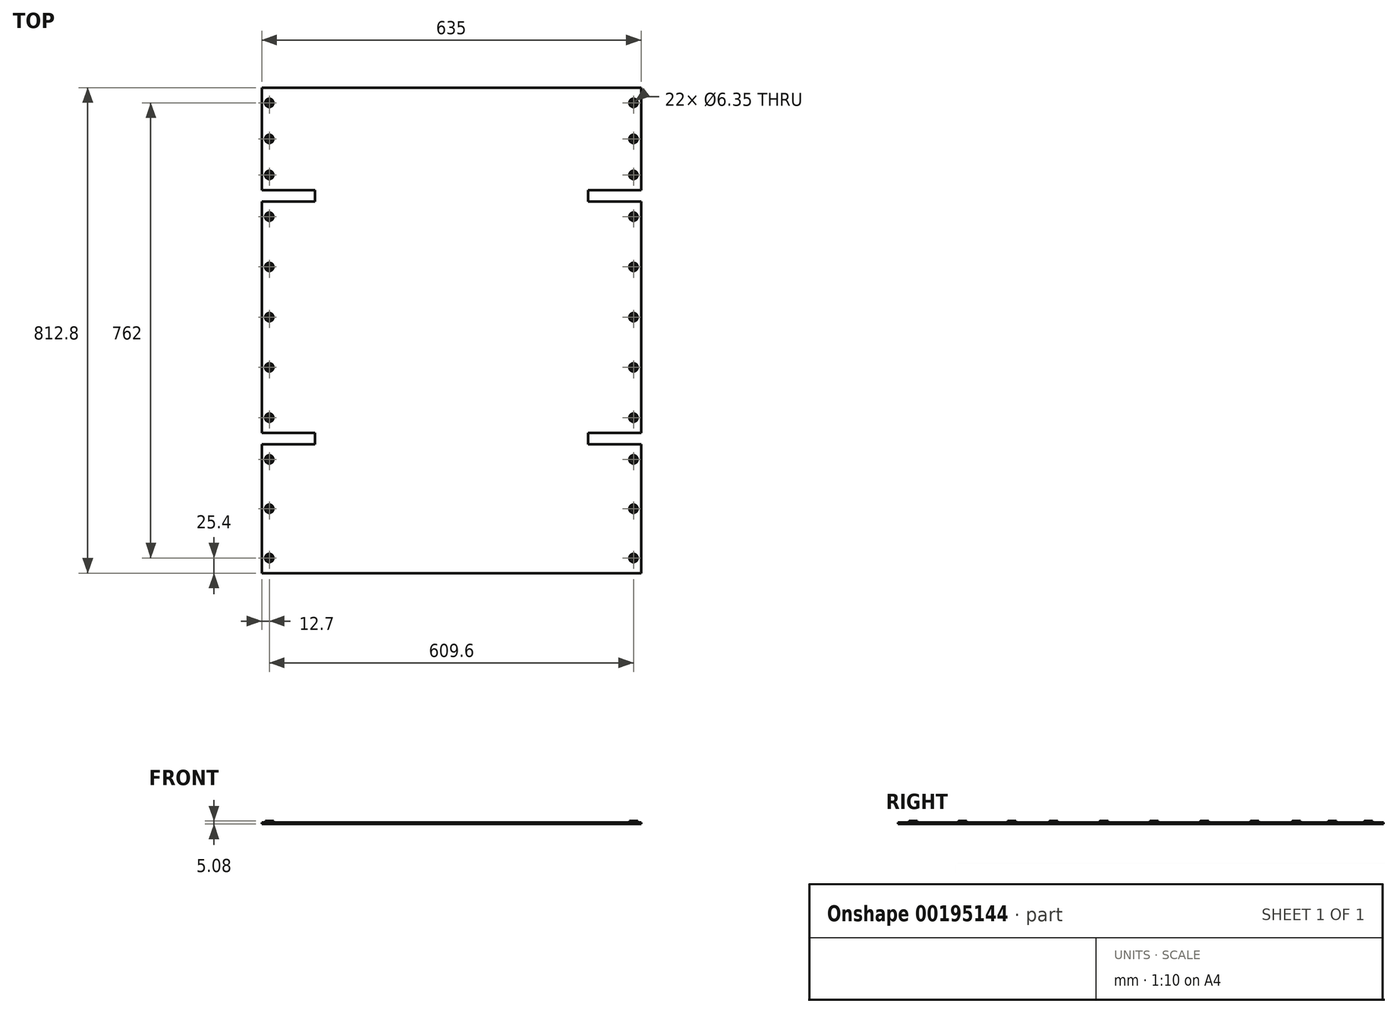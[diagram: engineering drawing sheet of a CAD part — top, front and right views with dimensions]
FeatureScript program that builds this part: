
annotation { "Feature Type Name" : "Feature", "Feature Type Description" : "" }
export const myFeature = defineFeature(function(context is Context, id is Id, definition is map)
    precondition{}
    {
        {
            var Q0;
            Q0=qCreatedBy(makeId("Top.planeOp"),FACE);
            var sketch = newSketch(context, id + "F0", { "sketchPlane" : qUnion([Q0])});
            skLineSegment(sketch, "E0.bottom", {"start": v(317.5, -406.4) * mm, "end": v(-317.5, -406.4) * mm});
            skLineSegment(sketch, "E0.top", {"start": v(317.5, 406.4) * mm, "end": v(-317.5, 406.4) * mm});
            skLineSegment(sketch, "E0.left", {"start": v(317.5, -406.4) * mm, "end": v(317.5, -190.5) * mm});
            skLineSegment(sketch, "E0.right", {"start": v(-317.5, -406.4) * mm, "end": v(-317.5, -190.5) * mm});
            skPoint(sketch, "E0.middle", {"position": v(0, 0) * mm});
            skLineSegment(sketch, "E1.bottom", {"start": v(317.5, -190.5) * mm, "end": v(228.6, -190.5) * mm});
            skLineSegment(sketch, "E1.top", {"start": v(317.5, -171.45) * mm, "end": v(228.6, -171.45) * mm});
            skLineSegment(sketch, "E1.right", {"start": v(228.6, -190.5) * mm, "end": v(228.6, -171.45) * mm});
            skLineSegment(sketch, "E2.bottom", {"start": v(317.5, 234.95) * mm, "end": v(228.6, 234.95) * mm});
            skLineSegment(sketch, "E2.top", {"start": v(317.5, 215.9) * mm, "end": v(228.6, 215.9) * mm});
            skLineSegment(sketch, "E2.right", {"start": v(228.6, 234.95) * mm, "end": v(228.6, 215.9) * mm});
            skLineSegment(sketch, "E3.trimOffspring", {"start": v(317.5, -171.45) * mm, "end": v(317.5, 215.9) * mm});
            skLineSegment(sketch, "E4.trimOffspring", {"start": v(317.5, 234.95) * mm, "end": v(317.5, 406.4) * mm});
            skCircle(sketch, "E5", {"center": v(304.8, -381) * mm, "radius": 3.18 * mm});
            skCircle(sketch, "E6", {"center": v(304.8, -298.45) * mm, "radius": 3.18 * mm});
            skCircle(sketch, "E7", {"center": v(304.8, -215.9) * mm, "radius": 3.18 * mm});
            skCircle(sketch, "E8", {"center": v(304.8, -146.05) * mm, "radius": 3.18 * mm});
            skCircle(sketch, "E9", {"center": v(304.8, -61.91) * mm, "radius": 3.18 * mm});
            skCircle(sketch, "E10", {"center": v(304.8, 22.22) * mm, "radius": 3.18 * mm});
            skCircle(sketch, "E11", {"center": v(304.8, 106.36) * mm, "radius": 3.18 * mm});
            skCircle(sketch, "E12", {"center": v(304.8, 190.5) * mm, "radius": 3.18 * mm});
            skCircle(sketch, "E13", {"center": v(304.8, 260.35) * mm, "radius": 3.18 * mm});
            skCircle(sketch, "E14", {"center": v(304.8, 320.67) * mm, "radius": 3.18 * mm});
            skCircle(sketch, "E15", {"center": v(304.8, 381) * mm, "radius": 3.18 * mm});
            skCircle(sketch, "E16.MirrorC", {"center": v(-304.8, 381) * mm, "radius": 3.18 * mm});
            skCircle(sketch, "E17.MirrorC", {"center": v(-304.8, 320.67) * mm, "radius": 3.18 * mm});
            skCircle(sketch, "E18.MirrorC", {"center": v(-304.8, 260.35) * mm, "radius": 3.18 * mm});
            skCircle(sketch, "E19.MirrorC", {"center": v(-304.8, 190.5) * mm, "radius": 3.18 * mm});
            skCircle(sketch, "E20.MirrorC", {"center": v(-304.8, 106.36) * mm, "radius": 3.18 * mm});
            skCircle(sketch, "E21.MirrorC", {"center": v(-304.8, 22.22) * mm, "radius": 3.18 * mm});
            skCircle(sketch, "E22.MirrorC", {"center": v(-304.8, -61.91) * mm, "radius": 3.18 * mm});
            skCircle(sketch, "E23.MirrorC", {"center": v(-304.8, -146.05) * mm, "radius": 3.18 * mm});
            skCircle(sketch, "E24.MirrorC", {"center": v(-304.8, -215.9) * mm, "radius": 3.18 * mm});
            skCircle(sketch, "E25.MirrorC", {"center": v(-304.8, -298.45) * mm, "radius": 3.18 * mm});
            skCircle(sketch, "E26.MirrorC", {"center": v(-304.8, -381) * mm, "radius": 3.18 * mm});
            skLineSegment(sketch, "E27.MirrorCS", {"start": v(-317.5, 215.9) * mm, "end": v(-228.6, 215.9) * mm});
            skLineSegment(sketch, "E28.MirrorCS", {"start": v(-317.5, 234.95) * mm, "end": v(-228.6, 234.95) * mm});
            skLineSegment(sketch, "E29.MirrorCS", {"start": v(-228.6, 234.95) * mm, "end": v(-228.6, 215.9) * mm});
            skLineSegment(sketch, "E30.MirrorCS", {"start": v(-317.5, -190.5) * mm, "end": v(-228.6, -190.5) * mm});
            skLineSegment(sketch, "E31.MirrorCS", {"start": v(-317.5, -171.45) * mm, "end": v(-228.6, -171.45) * mm});
            skLineSegment(sketch, "E32.MirrorCS", {"start": v(-228.6, -190.5) * mm, "end": v(-228.6, -171.45) * mm});
            skLineSegment(sketch, "E33.trimOffspring", {"start": v(-317.5, 234.95) * mm, "end": v(-317.5, 406.4) * mm});
            skLineSegment(sketch, "E34.trimOffspring", {"start": v(-317.5, -171.45) * mm, "end": v(-317.5, 215.9) * mm});
            skSolve(sketch);
        }
        {
            var Q0;
            Q0 = qSketchRegion(id + "F0", true);
            extrude(context, id + "F1", {"entities" : qUnion([Q0]), "depth" : 2.54 * mm});
        }
        {
            var Q0;
            Q0=makeQuery(id+"F1.opExtrude","CAP_FACE",FACE,{"disambiguationData":[OSD([sQuery(id+"F0.wireOp",EDGE,"E0.bottom"),sQuery(id+"F0.wireOp",EDGE,"E0.top"),sQuery(id+"F0.wireOp",EDGE,"E0.left"),sQuery(id+"F0.wireOp",EDGE,"E0.right"),sQuery(id+"F0.wireOp",EDGE,"E1.bottom"),sQuery(id+"F0.wireOp",EDGE,"E1.top"),sQuery(id+"F0.wireOp",EDGE,"E1.right"),sQuery(id+"F0.wireOp",EDGE,"E2.bottom"),sQuery(id+"F0.wireOp",EDGE,"E2.top"),sQuery(id+"F0.wireOp",EDGE,"E2.right"),sQuery(id+"F0.wireOp",EDGE,"E3.trimOffspring"),sQuery(id+"F0.wireOp",EDGE,"E4.trimOffspring"),sQuery(id+"F0.wireOp",EDGE,"E5"),sQuery(id+"F0.wireOp",EDGE,"E6"),sQuery(id+"F0.wireOp",EDGE,"E7"),sQuery(id+"F0.wireOp",EDGE,"E8"),sQuery(id+"F0.wireOp",EDGE,"E9"),sQuery(id+"F0.wireOp",EDGE,"E10"),sQuery(id+"F0.wireOp",EDGE,"E11"),sQuery(id+"F0.wireOp",EDGE,"E12"),sQuery(id+"F0.wireOp",EDGE,"E13"),sQuery(id+"F0.wireOp",EDGE,"E14"),sQuery(id+"F0.wireOp",EDGE,"E15"),sQuery(id+"F0.wireOp",EDGE,"E16.MirrorC"),sQuery(id+"F0.wireOp",EDGE,"E17.MirrorC"),sQuery(id+"F0.wireOp",EDGE,"E18.MirrorC"),sQuery(id+"F0.wireOp",EDGE,"E19.MirrorC"),sQuery(id+"F0.wireOp",EDGE,"E20.MirrorC"),sQuery(id+"F0.wireOp",EDGE,"E21.MirrorC"),sQuery(id+"F0.wireOp",EDGE,"E22.MirrorC"),sQuery(id+"F0.wireOp",EDGE,"E23.MirrorC"),sQuery(id+"F0.wireOp",EDGE,"E24.MirrorC"),sQuery(id+"F0.wireOp",EDGE,"E25.MirrorC"),sQuery(id+"F0.wireOp",EDGE,"E26.MirrorC"),sQuery(id+"F0.wireOp",EDGE,"E27.MirrorCS"),sQuery(id+"F0.wireOp",EDGE,"E28.MirrorCS"),sQuery(id+"F0.wireOp",EDGE,"E29.MirrorCS"),sQuery(id+"F0.wireOp",EDGE,"E30.MirrorCS"),sQuery(id+"F0.wireOp",EDGE,"E31.MirrorCS"),sQuery(id+"F0.wireOp",EDGE,"E32.MirrorCS"),sQuery(id+"F0.wireOp",EDGE,"E33.trimOffspring"),sQuery(id+"F0.wireOp",EDGE,"E34.trimOffspring")])],"isStart":false});
            var sketch = newSketch(context, id + "F2", { "sketchPlane" : qUnion([Q0])});
            skCircle(sketch, "E35", {"center": v(304.8, -381) * mm, "radius": 6.99 * mm});
            skCircle(sketch, "E36", {"center": v(304.8, -298.45) * mm, "radius": 6.99 * mm});
            skCircle(sketch, "E37", {"center": v(304.8, -215.9) * mm, "radius": 6.99 * mm});
            skCircle(sketch, "E38", {"center": v(304.8, -146.05) * mm, "radius": 6.99 * mm});
            skCircle(sketch, "E39", {"center": v(304.8, -61.91) * mm, "radius": 6.99 * mm});
            skCircle(sketch, "E40", {"center": v(304.8, 22.22) * mm, "radius": 6.99 * mm});
            skCircle(sketch, "E41", {"center": v(304.8, 106.36) * mm, "radius": 6.99 * mm});
            skCircle(sketch, "E42", {"center": v(304.8, 190.5) * mm, "radius": 6.99 * mm});
            skCircle(sketch, "E43", {"center": v(304.8, 260.35) * mm, "radius": 6.99 * mm});
            skCircle(sketch, "E44", {"center": v(304.8, 320.67) * mm, "radius": 6.99 * mm});
            skCircle(sketch, "E45", {"center": v(304.8, 381) * mm, "radius": 6.99 * mm});
            skCircle(sketch, "E46.MirrorC", {"center": v(-304.8, 381) * mm, "radius": 6.99 * mm});
            skCircle(sketch, "E47.MirrorC", {"center": v(-304.8, 320.67) * mm, "radius": 6.99 * mm});
            skCircle(sketch, "E48.MirrorC", {"center": v(-304.8, 260.35) * mm, "radius": 6.99 * mm});
            skCircle(sketch, "E49.MirrorC", {"center": v(-304.8, 190.5) * mm, "radius": 6.99 * mm});
            skCircle(sketch, "E50.MirrorC", {"center": v(-304.8, 106.36) * mm, "radius": 6.99 * mm});
            skCircle(sketch, "E51.MirrorC", {"center": v(-304.8, 22.22) * mm, "radius": 6.99 * mm});
            skCircle(sketch, "E52.MirrorC", {"center": v(-304.8, -61.91) * mm, "radius": 6.99 * mm});
            skCircle(sketch, "E53.MirrorC", {"center": v(-304.8, -146.05) * mm, "radius": 6.99 * mm});
            skCircle(sketch, "E54.MirrorC", {"center": v(-304.8, -215.9) * mm, "radius": 6.99 * mm});
            skCircle(sketch, "E55.MirrorC", {"center": v(-304.8, -298.45) * mm, "radius": 6.99 * mm});
            skCircle(sketch, "E56.MirrorC", {"center": v(-304.8, -381) * mm, "radius": 6.99 * mm});
            skCircle(sketch, "E57", {"center": v(304.8, -381) * mm, "radius": 3.18 * mm});
            skCircle(sketch, "E58", {"center": v(304.8, -298.45) * mm, "radius": 3.18 * mm});
            skCircle(sketch, "E59", {"center": v(304.8, -215.9) * mm, "radius": 3.18 * mm});
            skCircle(sketch, "E60", {"center": v(304.8, -146.05) * mm, "radius": 3.18 * mm});
            skCircle(sketch, "E61", {"center": v(304.8, -61.91) * mm, "radius": 3.18 * mm});
            skCircle(sketch, "E62", {"center": v(304.8, 22.22) * mm, "radius": 3.18 * mm});
            skCircle(sketch, "E63", {"center": v(304.8, 106.36) * mm, "radius": 3.18 * mm});
            skCircle(sketch, "E64", {"center": v(304.8, 190.5) * mm, "radius": 3.18 * mm});
            skCircle(sketch, "E65", {"center": v(304.8, 260.35) * mm, "radius": 3.18 * mm});
            skCircle(sketch, "E66", {"center": v(304.8, 320.67) * mm, "radius": 3.18 * mm});
            skCircle(sketch, "E67", {"center": v(304.8, 381) * mm, "radius": 3.18 * mm});
            skCircle(sketch, "E68.MirrorC", {"center": v(-304.8, 381) * mm, "radius": 3.18 * mm});
            skCircle(sketch, "E69.MirrorC", {"center": v(-304.8, 320.67) * mm, "radius": 3.18 * mm});
            skCircle(sketch, "E70.MirrorC", {"center": v(-304.8, 260.35) * mm, "radius": 3.18 * mm});
            skCircle(sketch, "E71.MirrorC", {"center": v(-304.8, 190.5) * mm, "radius": 3.18 * mm});
            skCircle(sketch, "E72.MirrorC", {"center": v(-304.8, 106.36) * mm, "radius": 3.18 * mm});
            skCircle(sketch, "E73.MirrorC", {"center": v(-304.8, 22.22) * mm, "radius": 3.18 * mm});
            skCircle(sketch, "E74.MirrorC", {"center": v(-304.8, -61.91) * mm, "radius": 3.18 * mm});
            skCircle(sketch, "E75.MirrorC", {"center": v(-304.8, -146.05) * mm, "radius": 3.18 * mm});
            skCircle(sketch, "E76.MirrorC", {"center": v(-304.8, -215.9) * mm, "radius": 3.18 * mm});
            skCircle(sketch, "E77.MirrorC", {"center": v(-304.8, -298.45) * mm, "radius": 3.18 * mm});
            skCircle(sketch, "E78.MirrorC", {"center": v(-304.8, -381) * mm, "radius": 3.18 * mm});
            skSolve(sketch);
        }
        {
            var Q0;
            Q0 = qSketchRegion(id + "F2", true);
            extrude(context, id + "F3", {"entities" : qUnion([Q0]), "operationType" : NewBodyOperationType.ADD, "depth" : 2.54 * mm});
        }
    });
